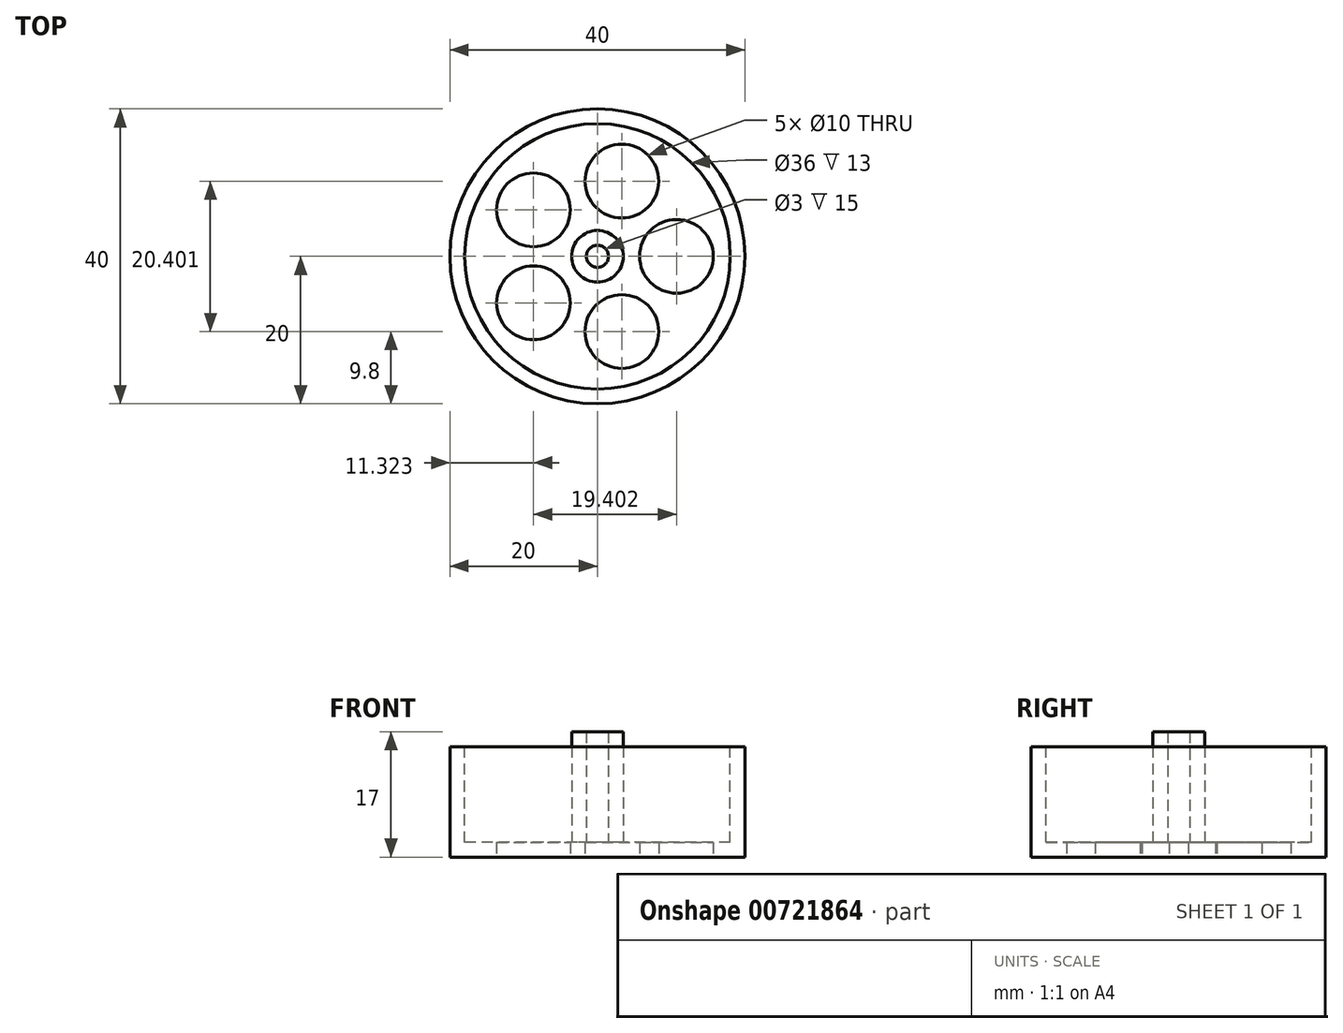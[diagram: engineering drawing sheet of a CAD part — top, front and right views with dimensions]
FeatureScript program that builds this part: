
annotation { "Feature Type Name" : "Feature", "Feature Type Description" : "" }
export const myFeature = defineFeature(function(context is Context, id is Id, definition is map)
    precondition{}
    {
        {
            var Q0;
            Q0=qCreatedBy(makeId("Top.planeOp"),FACE);
            var sketch = newSketch(context, id + "F0", { "sketchPlane" : qUnion([Q0])});
            skCircle(sketch, "E0", {"center": v(0, 0) * mm, "radius": 20 * mm});
            skSolve(sketch);
        }
        {
            var Q0;
            Q0=makeQuery(id+"F0.imprint","IMPRINT",FACE,{"disambiguationData":[TD([[makeQuery(id+"F0.imprint","IMPRINT",EDGE,{"derivedFrom":sQuery(id+"F0.wireOp",EDGE,"E0")}),1.0]])]});
            extrude(context, id + "F1", {"entities" : qUnion([Q0]), "depth" : 15 * mm, "offsetDistance" : 25 * mm});
        }
        {
            var Q0;
            Q0=makeQuery(id+"F1.opExtrude","CAP_FACE",FACE,{"disambiguationData":[OSD([sQuery(id+"F0.wireOp",EDGE,"E0")])],"isStart":false});
            var sketch = newSketch(context, id + "F2", { "sketchPlane" : qUnion([Q0])});
            skCircle(sketch, "E1", {"center": v(0, 0) * mm, "radius": 18 * mm});
            skSolve(sketch);
        }
        {
            var Q0;
            Q0=makeQuery(id+"F2.imprint","IMPRINT",FACE,{"disambiguationData":[TD([[makeQuery(id+"F2.imprint","IMPRINT",EDGE,{"derivedFrom":sQuery(id+"F2.wireOp",EDGE,"E1")}),1.0]])]});
            extrude(context, id + "F3", {"entities" : qUnion([Q0]), "operationType" : NewBodyOperationType.REMOVE, "oppositeDirection" : true, "depth" : 13 * mm, "offsetDistance" : 25 * mm});
        }
        {
            var Q0;
            Q0=makeQuery(id+"F3.boolean.opBoolean","COPY",FACE,{"derivedFrom":makeQuery(id+"F3.opExtrude","CAP_FACE",FACE,{"disambiguationData":[OSD([sQuery(id+"F2.wireOp",EDGE,"E1")])],"isStart":false})});
            var sketch = newSketch(context, id + "F4", { "sketchPlane" : qUnion([Q0])});
            skCircle(sketch, "E2", {"center": v(0, 0) * mm, "radius": 1.5 * mm});
            skCircle(sketch, "E3", {"center": v(0, 0) * mm, "radius": 3.5 * mm});
            skSolve(sketch);
        }
        {
            var Q0;
            Q0=makeQuery(id+"F4.imprint","IMPRINT",FACE,{"disambiguationData":[TD([[makeQuery(id+"F4.imprint","IMPRINT",EDGE,{"derivedFrom":sQuery(id+"F4.wireOp",EDGE,"E2")}),-1.0]])]});
            extrude(context, id + "F5", {"entities" : qUnion([Q0]), "operationType" : NewBodyOperationType.ADD, "depth" : 15 * mm, "offsetDistance" : 25 * mm});
        }
        {
            var Q0;
            Q0=makeQuery(id+"F1.opExtrude","CAP_FACE",FACE,{"disambiguationData":[OSD([sQuery(id+"F0.wireOp",EDGE,"E0")])],"isStart":true});
            var sketch = newSketch(context, id + "F6", { "sketchPlane" : qUnion([Q0])});
            skCircle(sketch, "E4", {"center": v(10.73, 0) * mm, "radius": 5 * mm});
            skCircle(sketch, "E5.1.0", {"center": v(3.31, 10.2) * mm, "radius": 5 * mm});
            skCircle(sketch, "E5.2.0", {"center": v(-8.68, 6.3) * mm, "radius": 5 * mm});
            skCircle(sketch, "E5.3.0", {"center": v(-8.68, -6.3) * mm, "radius": 5 * mm});
            skCircle(sketch, "E5.4.0", {"center": v(3.31, -10.2) * mm, "radius": 5 * mm});
            skPoint(sketch, "E5.center", {"position": v(0, 0) * mm});
            skSolve(sketch);
        }
        {
            var Q0;
            Q0=makeQuery(id+"F6.imprint","IMPRINT",FACE,{"disambiguationData":[TD([[makeQuery(id+"F6.imprint","IMPRINT",EDGE,{"derivedFrom":sQuery(id+"F6.wireOp",EDGE,"E4")}),1.0]])]});
            var Q1;
            Q1=makeQuery(id+"F6.imprint","IMPRINT",FACE,{"disambiguationData":[TD([[makeQuery(id+"F6.imprint","IMPRINT",EDGE,{"derivedFrom":sQuery(id+"F6.wireOp",EDGE,"E5.4.0")}),1.0]])]});
            var Q2;
            Q2=makeQuery(id+"F6.imprint","IMPRINT",FACE,{"disambiguationData":[TD([[makeQuery(id+"F6.imprint","IMPRINT",EDGE,{"derivedFrom":sQuery(id+"F6.wireOp",EDGE,"E5.3.0")}),1.0]])]});
            var Q3;
            Q3=makeQuery(id+"F6.imprint","IMPRINT",FACE,{"disambiguationData":[TD([[makeQuery(id+"F6.imprint","IMPRINT",EDGE,{"derivedFrom":sQuery(id+"F6.wireOp",EDGE,"E5.2.0")}),1.0]])]});
            var Q4;
            Q4=makeQuery(id+"F6.imprint","IMPRINT",FACE,{"disambiguationData":[TD([[makeQuery(id+"F6.imprint","IMPRINT",EDGE,{"derivedFrom":sQuery(id+"F6.wireOp",EDGE,"E5.1.0")}),1.0]])]});
            extrude(context, id + "F7", {"entities" : qUnion([Q0, Q1, Q2, Q3, Q4]), "operationType" : NewBodyOperationType.REMOVE, "oppositeDirection" : true, "depth" : 2 * mm, "offsetDistance" : 25 * mm});
        }
    });
